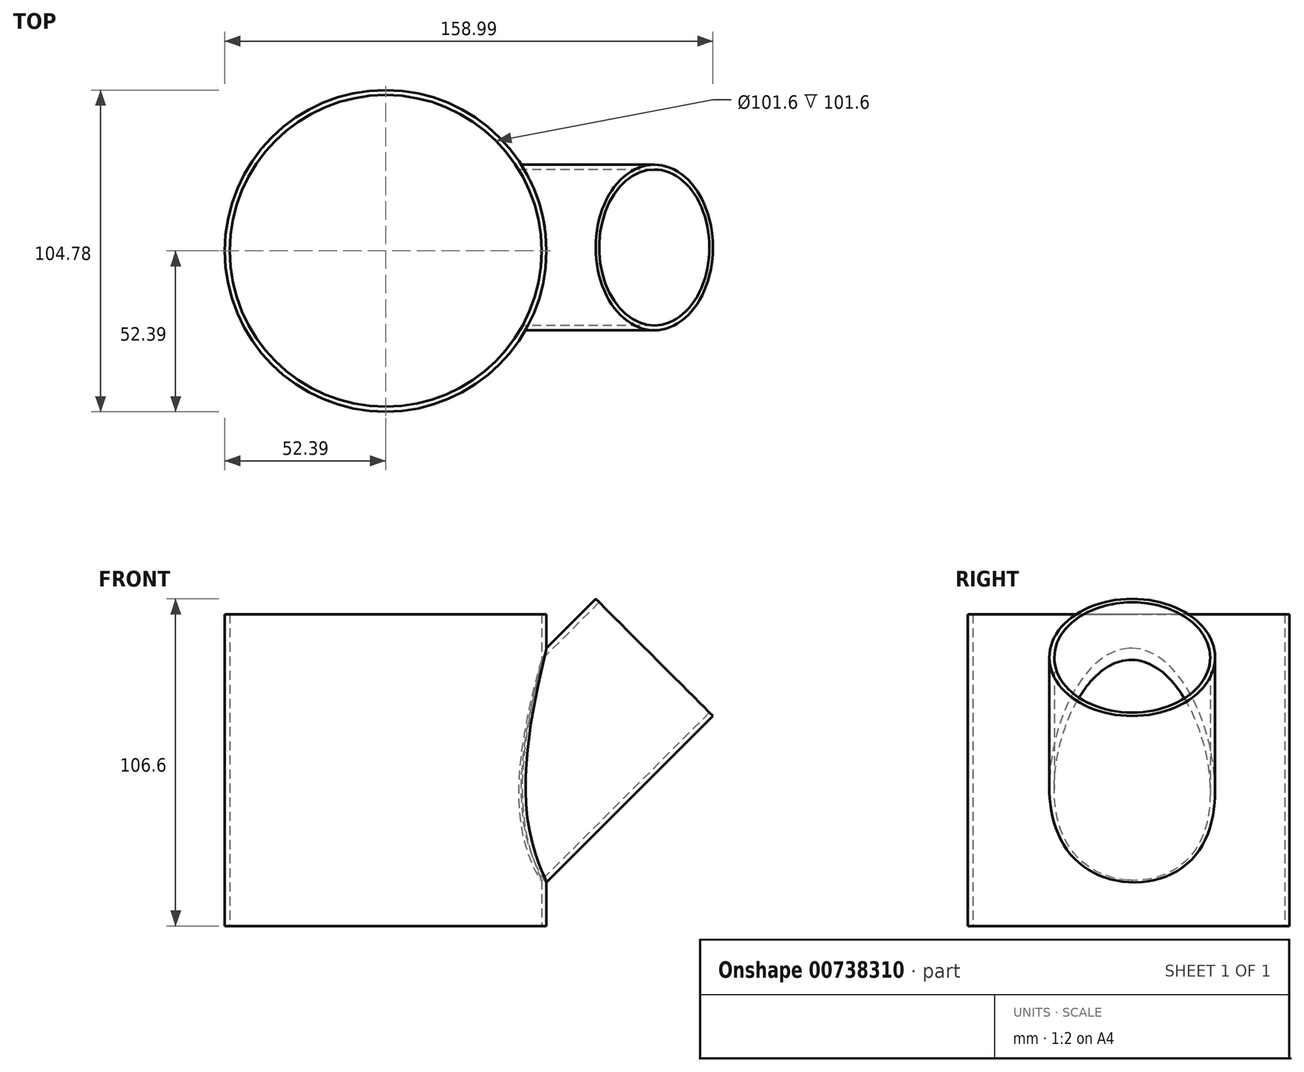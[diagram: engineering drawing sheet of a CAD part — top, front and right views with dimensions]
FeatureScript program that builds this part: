
annotation { "Feature Type Name" : "Feature", "Feature Type Description" : "" }
export const myFeature = defineFeature(function(context is Context, id is Id, definition is map)
    precondition{}
    {
        {
            var Q0;
            Q0=qCreatedBy(makeId("Top.planeOp"),FACE);
            var sketch = newSketch(context, id + "F0", { "sketchPlane" : qUnion([Q0])});
            skCircle(sketch, "E0", {"center": v(0, 0) * mm, "radius": 50.8 * mm});
            skCircle(sketch, "E1", {"center": v(0, 0) * mm, "radius": 52.39 * mm});
            skSolve(sketch);
        }
        {
            var Q0;
            Q0=qSketchRegion(id+"F0",true);
            extrude(context, id + "F1", {"entities" : qUnion([Q0]), "depth" : 101.6 * mm});
        }
        {
            var Q0;
            Q0=qCreatedBy(makeId("Top.planeOp"),FACE);
            cPlane(context, id + "F2", {"entities" : qUnion([Q0]), "cplaneType" : CPlaneType.OFFSET, "offset" : 50.8 * mm, "width" : 152.4 * mm, "height" : 152.4 * mm});
        }
        {
            var Q0;
            Q0=qCreatedBy(id+"F2.planeOp",FACE);
            var sketch = newSketch(context, id + "F3", { "sketchPlane" : qUnion([Q0])});
            skCircle(sketch, "E2.0", {"center": v(0, 0) * mm, "radius": 52.39 * mm, "construction": true});
            skLineSegment(sketch, "E3", {"start": v(0, 0) * mm, "end": v(52.39, 0) * mm, "construction": true});
            skLineSegment(sketch, "E4", {"start": v(52.39, 0) * mm, "end": v(52.39, 56) * mm});
            skSolve(sketch);
        }
        {
            var Q0;
            Q0=sQuery(id+"F3.wireOp",EDGE,"E4");
            cPlane(context, id + "F4", {"entities" : qUnion([Q0]), "cplaneType" : CPlaneType.LINE_ANGLE, "offset" : 25.4 * mm, "angle" : 45 * degree, "width" : 152.4 * mm, "height" : 152.4 * mm});
        }
        {
            var Q0;
            Q0=qCreatedBy(id+"F4.planeOp",FACE);
            var sketch = newSketch(context, id + "F5", { "sketchPlane" : qUnion([Q0])});
            skPoint(sketch, "E5.0", {"position": v(1.12, 0) * mm});
            skCircle(sketch, "E6", {"center": v(1.12, 0) * mm, "radius": 25.4 * mm});
            skCircle(sketch, "E7", {"center": v(1.12, 0) * mm, "radius": 26.99 * mm});
            skSolve(sketch);
        }
        {
            var Q0;
            Q0=makeQuery(id+"F5.imprint","IMPRINT",FACE,{"disambiguationData":[TD([[makeQuery(id+"F5.imprint","IMPRINT",EDGE,{"derivedFrom":sQuery(id+"F5.wireOp",EDGE,"E6")}),-1.0]])]});
            extrude(context, id + "F6", {"entities" : qUnion([Q0]), "operationType" : NewBodyOperationType.ADD, "depth" : 50.8 * mm, "hasSecondDirection" : true, "secondDirectionOppositeDirection" : true, "secondDirectionDepth" : 50.8 * mm, "offsetDistance" : 25.4 * mm});
        }
        {
            var Q0;
            Q0=makeQuery(id+"F0.imprint","IMPRINT",FACE,{"disambiguationData":[TD([[makeQuery(id+"F0.imprint","IMPRINT",EDGE,{"derivedFrom":sQuery(id+"F0.wireOp",EDGE,"E0")}),1.0]])]});
            extrude(context, id + "F7", {"entities" : qUnion([Q0]), "operationType" : NewBodyOperationType.REMOVE, "endBound" : BoundingType.THROUGH_ALL, "depth" : 271.78 * mm, "hasSecondDirection" : true, "secondDirectionBound" : SecondDirectionBoundingType.THROUGH_ALL, "secondDirectionOppositeDirection" : true, "secondDirectionDepth" : 25.4 * mm, "offsetDistance" : 25.4 * mm});
        }
        {
            var Q0;
            Q0=makeQuery(id+"F5.imprint","IMPRINT",FACE,{"disambiguationData":[TD([[makeQuery(id+"F5.imprint","IMPRINT",EDGE,{"derivedFrom":sQuery(id+"F5.wireOp",EDGE,"E6")}),1.0]])]});
            extrude(context, id + "F8", {"entities" : qUnion([Q0]), "operationType" : NewBodyOperationType.REMOVE, "oppositeDirection" : true, "depth" : 50.8 * mm, "hasSecondDirection" : true, "secondDirectionBound" : SecondDirectionBoundingType.THROUGH_ALL, "secondDirectionOppositeDirection" : false, "secondDirectionDepth" : 25.4 * mm, "offsetDistance" : 25.4 * mm});
        }
    });
